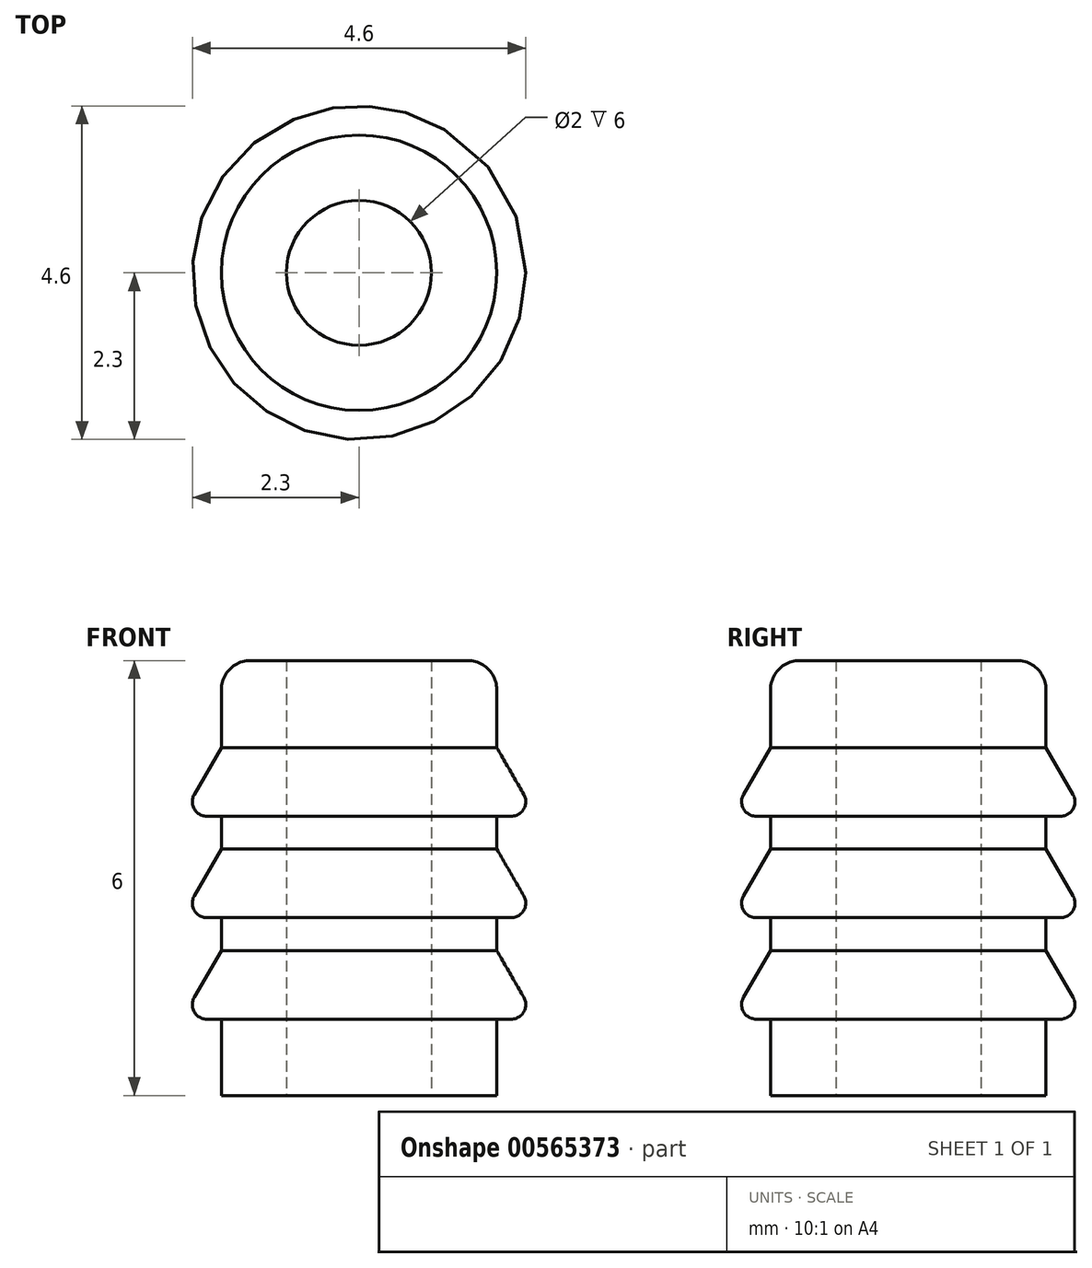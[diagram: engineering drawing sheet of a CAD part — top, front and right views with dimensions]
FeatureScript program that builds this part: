
annotation { "Feature Type Name" : "Feature", "Feature Type Description" : "" }
export const myFeature = defineFeature(function(context is Context, id is Id, definition is map)
    precondition{}
    {
        {
            var Q0;
            Q0=qCreatedBy(makeId("Top.planeOp"),FACE);
            var sketch = newSketch(context, id + "F0", { "sketchPlane" : qUnion([Q0])});
            skCircle(sketch, "E0", {"center": v(0, 0) * mm, "radius": 1.9 * mm});
            skCircle(sketch, "E1", {"center": v(0, 0) * mm, "radius": 1 * mm});
            skSolve(sketch);
        }
        {
            var Q0;
            Q0=qSketchRegion(id+"F0",true);
            extrude(context, id + "F1", {"entities" : qUnion([Q0]), "depth" : 6 * mm});
        }
        {
            var Q0;
            Q0=makeQuery(id+"F1.opExtrude","CAP_EDGE",EDGE,{"disambiguationData":[OSD([sQuery(id+"F0.wireOp",EDGE,"E0")])],"isStart":false});
            fillet(context, id + "F2", {"entities" : qUnion([Q0]), "radius" : 0.4 * mm, "tangentPropagation" : true, "allowEdgeOverflow" : false});
        }
        {
            var Q0;
            Q0=qCreatedBy(makeId("Front.planeOp"),FACE);
            var sketch = newSketch(context, id + "F3", { "sketchPlane" : qUnion([Q0])});
            skLineSegment(sketch, "E2.0", {"start": v(-1.5, 6) * mm, "end": v(1.5, 6) * mm, "construction": true});
            skLineSegment(sketch, "E3", {"start": v(-1.9, 4.8) * mm, "end": v(-2.27, 4.15) * mm});
            skLineSegment(sketch, "E4", {"start": v(-2.1, 3.85) * mm, "end": v(-1.9, 3.85) * mm});
            skLineSegment(sketch, "E5", {"start": v(-1.9, 3.85) * mm, "end": v(-1.9, 4.8) * mm});
            skLineSegment(sketch, "E6", {"start": v(0, 7.66) * mm, "end": v(0, -1.98) * mm, "construction": true});
            skPoint(sketch, "E7.visualSharp", {"position": v(-2.45, 3.85) * mm});
            skArc(sketch, "E7.filletArc", {"start": v(-2.27, 4.15) * mm, "mid": v(-2.27, 3.95) * mm, "end": v(-2.1, 3.85) * mm});
            skLineSegment(sketch, "E8.1.0.0", {"start": v(-1.9, 2.45) * mm, "end": v(-1.9, 3.4) * mm});
            skLineSegment(sketch, "E8.1.0.1", {"start": v(-1.9, 3.4) * mm, "end": v(-2.27, 2.75) * mm});
            skArc(sketch, "E8.1.0.2", {"start": v(-2.27, 2.75) * mm, "mid": v(-2.27, 2.55) * mm, "end": v(-2.1, 2.45) * mm});
            skLineSegment(sketch, "E8.1.0.3", {"start": v(-2.1, 2.45) * mm, "end": v(-1.9, 2.45) * mm});
            skLineSegment(sketch, "E8.2.0.0", {"start": v(-1.9, 1.05) * mm, "end": v(-1.9, 2) * mm});
            skLineSegment(sketch, "E8.2.0.1", {"start": v(-1.9, 2) * mm, "end": v(-2.27, 1.35) * mm});
            skArc(sketch, "E8.2.0.2", {"start": v(-2.27, 1.35) * mm, "mid": v(-2.27, 1.15) * mm, "end": v(-2.1, 1.05) * mm});
            skLineSegment(sketch, "E8.2.0.3", {"start": v(-2.1, 1.05) * mm, "end": v(-1.9, 1.05) * mm});
            skLineSegment(sketch, "E8.direction1", {"start": v(-1.9, 3.85) * mm, "end": v(-1.9, 2.45) * mm, "construction": true});
            skSolve(sketch);
        }
        {
            var Q0;
            Q0=qSketchRegion(id+"F3",true);
            var Q1;
            Q1=sQuery(id+"F3.wireOp",EDGE,"E6");
            revolve(context, id + "F4", {"operationType" : NewBodyOperationType.ADD, "entities" : qUnion([Q0]), "axis" : qUnion([Q1]), "revolveType" : RevolveType.FULL});
        }
    });
